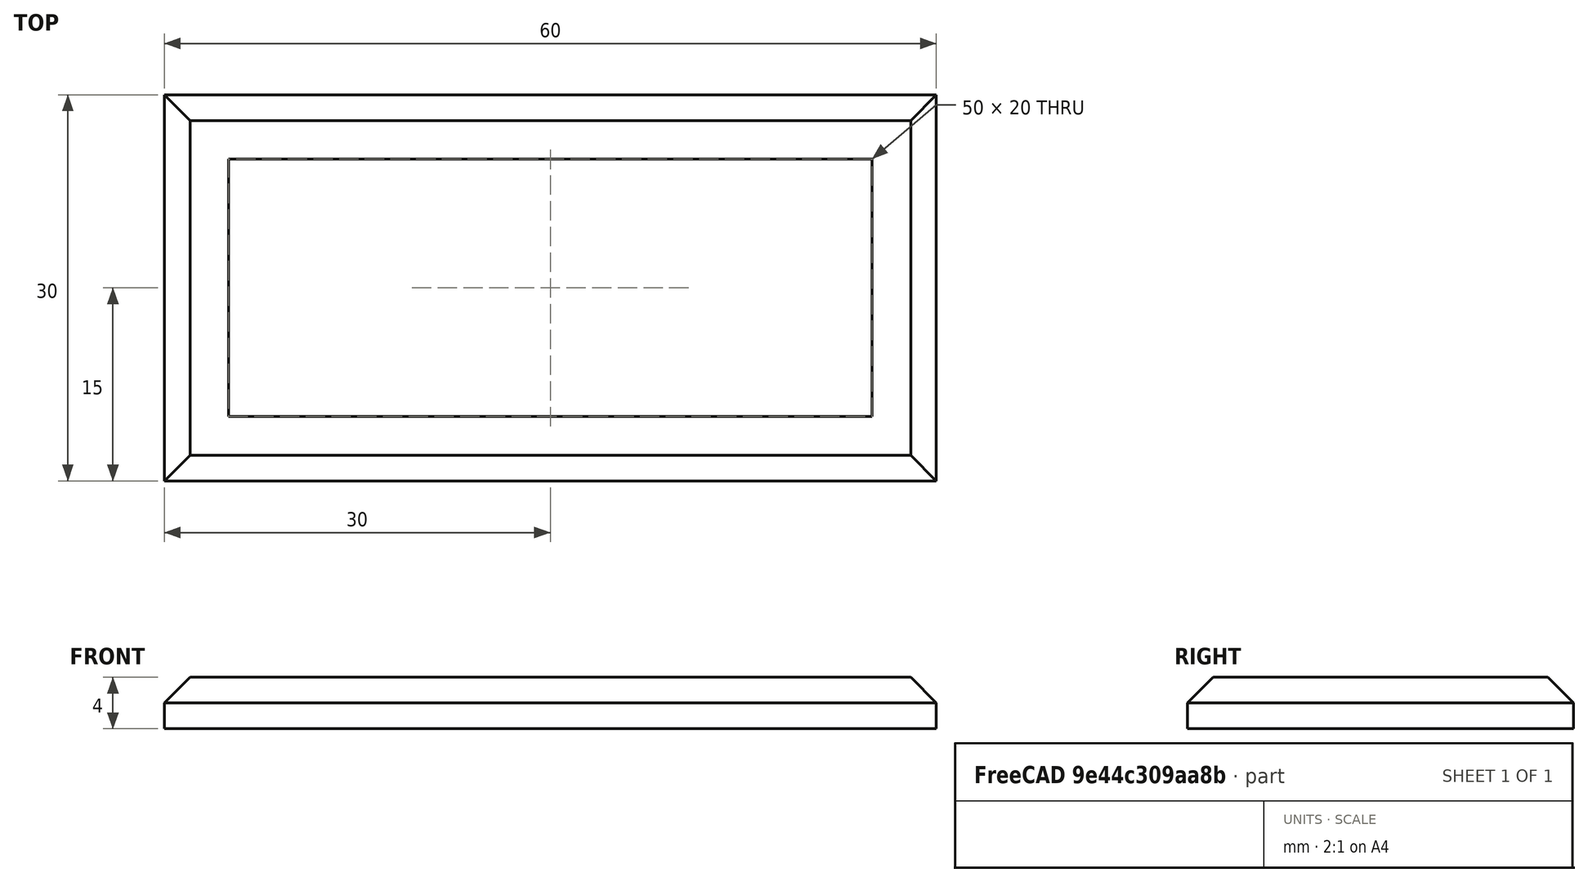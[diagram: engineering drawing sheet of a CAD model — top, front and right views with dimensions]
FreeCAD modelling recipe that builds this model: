
FCSTD DOCUMENT  (FreeCAD 0.17R13217 (Git))
Label: 04-1-marco
License: All rights reserved
LicenseURL: http://en.wikipedia.org/wiki/All_rights_reserved
objects: TechDraw::DrawViewDimension×7, TechDraw::DrawProjGroupItem×2, Sketcher::SketchObject×1, PartDesign::Pad×1, PartDesign::Chamfer×1, PartDesign::Body×1, TechDraw::DrawSVGTemplate×1, TechDraw::DrawProjGroup×1, TechDraw::DrawViewPart×1, TechDraw::DrawViewAnnotation×1, TechDraw::DrawPage×1
note: 5 computed .brp shape members not serialized (recipe doc carries the construction recipe); baked Part::Feature solids carry a one-line shape summary decoded from their .brp

FEATURE [Sketcher::SketchObject] Sketch
  MapMode = 5
  Support = -> [XY_Plane]
  sketch-geometry (9):
    g0: LineSegment StartX=-30 StartY=15 StartZ=0 EndX=30 EndY=15 EndZ=0
    g1: LineSegment StartX=30 StartY=15 StartZ=0 EndX=30 EndY=-15 EndZ=0
    g2: LineSegment StartX=30 StartY=-15 StartZ=0 EndX=-30 EndY=-15 EndZ=0
    g3: LineSegment StartX=-30 StartY=-15 StartZ=0 EndX=-30 EndY=15 EndZ=0
    g4: LineSegment StartX=-25 StartY=10 StartZ=0 EndX=25 EndY=10 EndZ=0
    g5: LineSegment StartX=25 StartY=10 StartZ=0 EndX=25 EndY=-10 EndZ=0
    g6: LineSegment StartX=25 StartY=-10 StartZ=0 EndX=-25 EndY=-10 EndZ=0
    g7: LineSegment StartX=-25 StartY=-10 StartZ=0 EndX=-25 EndY=10 EndZ=0
    g8: LineSegment [constr] StartX=-30 StartY=15 StartZ=0 EndX=-25 EndY=10 EndZ=0
  constraints (24):
    c: Coincident(g0,g1)
    c: Coincident(g1,g2)
    c: Coincident(g2,g3)
    c: Coincident(g3,g0)
    c: Horizontal(g0)
    c: Horizontal(g2)
    c: Vertical(g1)
    c: Vertical(g3)
    c: Symmetric(g0,g1,g-1)
    c: Coincident(g4,g5)
    c: Coincident(g5,g6)
    c: Coincident(g6,g7)
    c: Coincident(g7,g4)
    c: Horizontal(g4)
    c: Horizontal(g6)
    c: Vertical(g5)
    c: Vertical(g7)
    c: Symmetric(g4,g5,g-1)
    c: Coincident(g8,g0)
    c: Coincident(g8,g4)
    c: Angle(g8,g0) = 0.785398
    c: DistanceX(g0,g0) = 60
    c: DistanceY(g3,g3) = 30
    c: DistanceX(g0,g4) = 5
FEATURE [PartDesign::Pad] Pad
  Length = 4
  Length2 = 100
  Profile = -> Sketch
  Refine = true
  Type = 0
FEATURE [PartDesign::Chamfer] Chamfer
  Base = -> Pad [Edge10,Edge7,Edge4,Edge12]
  BaseFeature = -> Pad
  Size = 2
FEATURE [PartDesign::Body] Body
  Group = -> [Sketch,Pad,Chamfer]
  Origin = -> Origin
  Tip = -> Chamfer
FEATURE [TechDraw::DrawSVGTemplate] Template
  EditableTexts = Designed_by_Name=Designed by Name; Drawing_number=Drawing number; FC-Date=Date; FC-SC=Scale; FC-SH=Sheet; FC-Title=Title; Subtitle=Subtitle; Weight=Weight
  Height = 210
  Orientation = 1
  Width = 297
FEATURE [TechDraw::DrawProjGroupItem] ProjItem  label="Front"
  ArcCenterMarks = true
  CenterScale = 2
  CoarseView = false
  Direction = (0,-1,0)
  ExtraWidth = 1.4
  Focus = 100
  HardHidden = false
  HiddenWidth = 0.35
  HorizCenterLine = false
  IsoCount = 0
  IsoHidden = false
  IsoVisible = false
  IsoWidth = 0.5
  KeepLabel = false
  LineWidth = 0.7
  LockPosition = false
  Perspective = false
  Rotation = 0
  RotationVector = (1,0,0)
  ScaleType = 0
  SeamHidden = false
  SeamVisible = false
  ShowSectionLine = true
  SmoothHidden = false
  SmoothVisible = false
  Source = -> [Chamfer]
  Type = 0
  VertCenterLine = false
  X = 0
  Y = 0
FEATURE [TechDraw::DrawProjGroupItem] ProjItem001  label="Top"
  ArcCenterMarks = true
  CenterScale = 2
  CoarseView = false
  Direction = (0,0,1)
  ExtraWidth = 1.4
  Focus = 100
  HardHidden = false
  HiddenWidth = 0.35
  HorizCenterLine = false
  IsoCount = 0
  IsoHidden = false
  IsoVisible = false
  IsoWidth = 0.5
  KeepLabel = false
  LineWidth = 0.7
  LockPosition = false
  Perspective = false
  Rotation = 0
  RotationVector = (1,0,0)
  ScaleType = 0
  SeamHidden = false
  SeamVisible = false
  ShowSectionLine = true
  SmoothHidden = false
  SmoothVisible = false
  Source = -> [Chamfer]
  Type = 4
  VertCenterLine = false
  X = 0
  Y = -60
FEATURE [TechDraw::DrawProjGroup] ProjGroup
  Anchor = -> ProjItem
  AutoDistribute = true
  CubeDirs = (1) [(0,0,0)]
  CubeRotations = (1) [(0,0,0)]
  KeepLabel = false
  LockPosition = false
  ProjectionType = 0
  Rotation = 0
  Scale = 1.5
  ScaleType = 2
  Source = -> [Chamfer]
  Views = -> [ProjItem,ProjItem001]
  X = 80.7009
  Y = 159.495
  spacingX = 15
  spacingY = 15
FEATURE [TechDraw::DrawViewPart] View
  ArcCenterMarks = true
  CenterScale = 2
  CoarseView = false
  Direction = (1,1,1)
  ExtraWidth = 1.4
  Focus = 100
  HardHidden = false
  HiddenWidth = 0.35
  HorizCenterLine = false
  IsoCount = 0
  IsoHidden = false
  IsoVisible = false
  IsoWidth = 0.5
  KeepLabel = false
  LineWidth = 0.7
  LockPosition = false
  Perspective = false
  Rotation = 0
  Scale = 2
  ScaleType = 0
  SeamHidden = false
  SeamVisible = false
  ShowSectionLine = true
  SmoothHidden = false
  SmoothVisible = false
  Source = -> [Chamfer]
  VertCenterLine = false
  X = 218.5
  Y = 107.711
FEATURE [TechDraw::DrawViewDimension] Dimension
  Font = osifont
  Fontsize = 3.5
  FormatSpec = %.2f
  KeepLabel = false
  LineWidth = 0.5
  LockPosition = false
  MeasureType = 1
  References2D = -> [ProjItem]
  Rotation = 0
  Scale = 2
  ScaleType = 0
  Type = 2
  X = 55.9507
  Y = -12.0775
FEATURE [TechDraw::DrawViewDimension] Dimension001
  Font = osifont
  Fontsize = 3.5
  FormatSpec = %.2f
  KeepLabel = false
  LineWidth = 0.5
  LockPosition = false
  MeasureType = 1
  References2D = -> [ProjItem]
  Rotation = 0
  Scale = 2
  ScaleType = 0
  Type = 2
  X = -54.9648
  Y = -14.5423
FEATURE [TechDraw::DrawViewDimension] Dimension002
  Font = osifont
  Fontsize = 3.5
  FormatSpec = %.2f
  KeepLabel = false
  LineWidth = 0.5
  LockPosition = false
  MeasureType = 1
  References2D = -> [ProjItem001]
  Rotation = 0
  Scale = 2
  ScaleType = 0
  Type = 1
  X = -0.985915
  Y = 38.4507
FEATURE [TechDraw::DrawViewDimension] Dimension003
  Font = osifont
  Fontsize = 3.5
  FormatSpec = %.2f
  KeepLabel = false
  LineWidth = 0.5
  LockPosition = false
  MeasureType = 1
  References2D = -> [ProjItem001]
  Rotation = 0
  Scale = 2
  ScaleType = 0
  Type = 2
  X = 52.7465
  Y = 1.47887
FEATURE [TechDraw::DrawViewDimension] Dimension004
  Font = osifont
  Fontsize = 3.5
  FormatSpec = %.2f
  KeepLabel = false
  LineWidth = 0.5
  LockPosition = false
  MeasureType = 1
  References2D = -> [ProjItem001]
  Rotation = 0
  Scale = 2
  ScaleType = 0
  Type = 1
  X = -17.2535
  Y = -35.7394
FEATURE [TechDraw::DrawViewDimension] Dimension005
  Font = osifont
  Fontsize = 3.5
  FormatSpec = %.2f
  KeepLabel = false
  LineWidth = 0.5
  LockPosition = false
  MeasureType = 1
  References2D = -> [ProjItem001]
  Rotation = 0
  Scale = 2
  ScaleType = 0
  Type = 2
  X = -61.3732
  Y = -0.246479
FEATURE [TechDraw::DrawViewDimension] Dimension006
  Font = osifont
  Fontsize = 3.5
  FormatSpec = %.2f
  KeepLabel = false
  LineWidth = 0.5
  LockPosition = false
  MeasureType = 1
  References2D = -> [ProjItem]
  Rotation = 0
  Scale = 2
  ScaleType = 0
  Type = 6
  X = 19.9648
  Y = -10.1056
FEATURE [TechDraw::DrawViewAnnotation] Annotation
  Font = osifont
  KeepLabel = false
  LineSpace = 90
  LockPosition = false
  MaxWidth = -1
  Rotation = 0
  Scale = 2
  ScaleType = 0
  Text = Marco
  TextSize = 8
  TextStyle = 1
  X = 217.021
  Y = 176.232
FEATURE [TechDraw::DrawPage] Page
  KeepUpdated = true
  ProjectionType = 0
  Scale = 2
  Template = -> Template
  Views = -> [ProjGroup,View,Dimension,Dimension001,Dimension002,Dimension003,Dimension004,Dimension005,Dimension006,Annotation]
